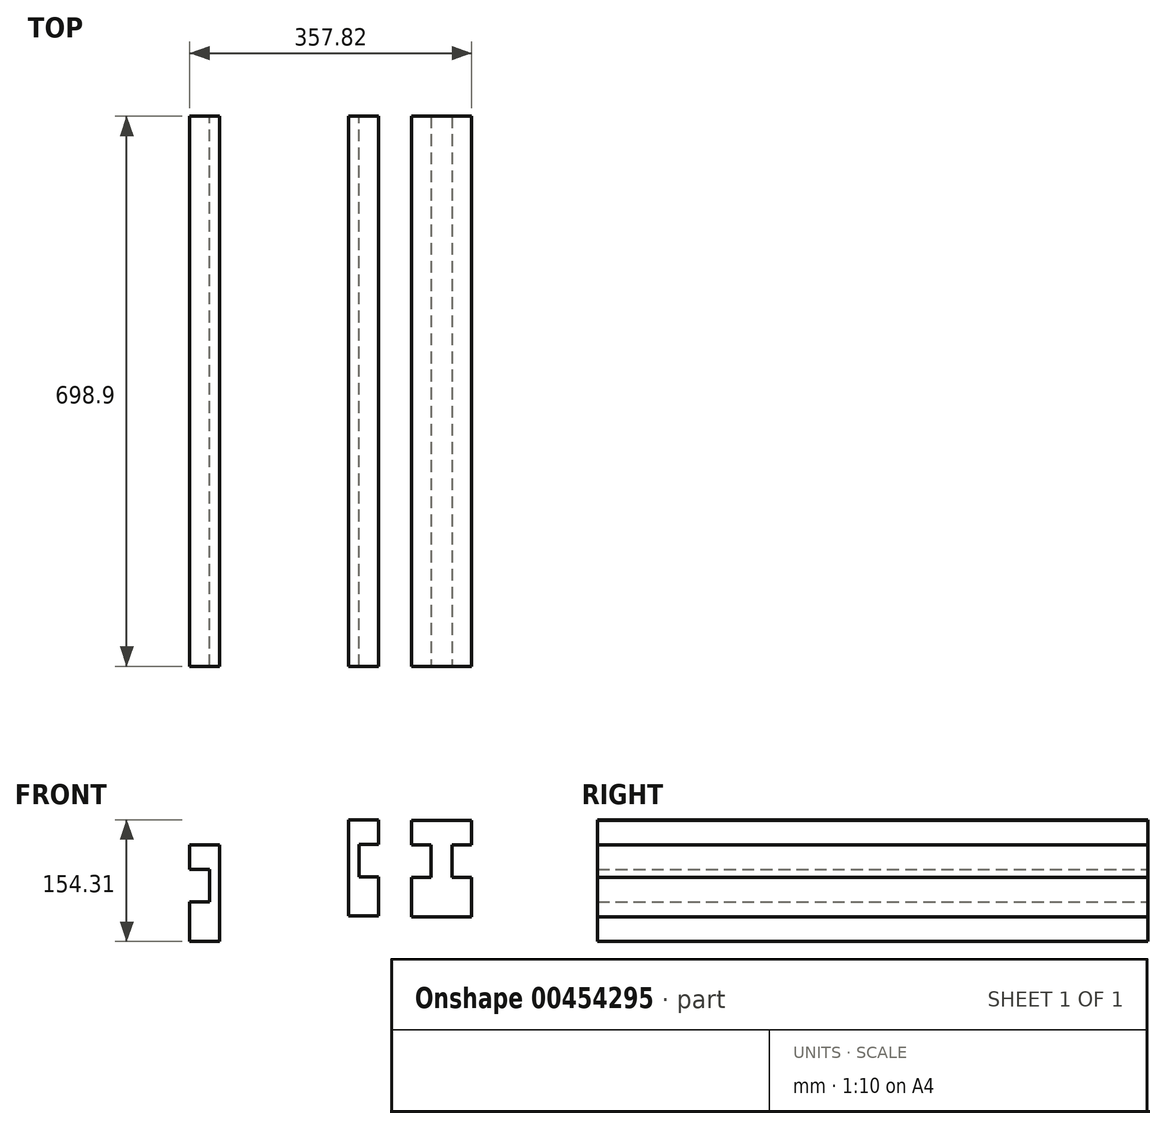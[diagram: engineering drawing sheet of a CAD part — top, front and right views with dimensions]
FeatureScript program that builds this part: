
annotation { "Feature Type Name" : "Feature", "Feature Type Description" : "" }
export const myFeature = defineFeature(function(context is Context, id is Id, definition is map)
    precondition{}
    {
        {
            var Q0;
            Q0=qCreatedBy(makeId("Front.planeOp"),FACE);
            var sketch = newSketch(context, id + "F0", { "sketchPlane" : qUnion([Q0])});
            skLineSegment(sketch, "E0.bottom", {"start": v(13.05, -61.15) * mm, "end": v(-13.05, -61.15) * mm});
            skLineSegment(sketch, "E0.top", {"start": v(13.05, 61.15) * mm, "end": v(-13.05, 61.15) * mm});
            skLineSegment(sketch, "E0.left", {"start": v(13.05, -61.15) * mm, "end": v(13.05, 61.15) * mm});
            skLineSegment(sketch, "E0.right", {"start": v(-13.05, -61.15) * mm, "end": v(-13.05, 61.15) * mm});
            skPoint(sketch, "E0.middle", {"position": v(0, 0) * mm});
            skSolve(sketch);
        }
        {
            var Q0;
            Q0=makeQuery(id+"F0.imprint","IMPRINT",FACE,{"disambiguationData":[TD([[makeQuery(id+"F0.imprint","IMPRINT",EDGE,{"derivedFrom":sQuery(id+"F0.wireOp",EDGE,"E0.bottom")}),-1.0]])]});
            extrude(context, id + "F1", {"entities" : qUnion([Q0]), "depth" : 698.9 * mm});
        }
        {
            var Q0;
            Q0=makeQuery(id+"F1.opExtrude","CAP_FACE",FACE,{"disambiguationData":[OSD([sQuery(id+"F0.wireOp",EDGE,"E0.bottom"),sQuery(id+"F0.wireOp",EDGE,"E0.top"),sQuery(id+"F0.wireOp",EDGE,"E0.left"),sQuery(id+"F0.wireOp",EDGE,"E0.right")])],"isStart":false});
            var sketch = newSketch(context, id + "F2", { "sketchPlane" : qUnion([Q0])});
            skLineSegment(sketch, "E1.bottom", {"start": v(-13.05, 61.15) * mm, "end": v(-38.05, 61.15) * mm});
            skLineSegment(sketch, "E2", {"start": v(0, 61.15) * mm, "end": v(0, -61.15) * mm, "construction": true});
            skPoint(sketch, "E3", {"position": v(-13.05, -11.15) * mm});
            skPoint(sketch, "E4", {"position": v(-13.05, 30.05) * mm});
            skLineSegment(sketch, "E5", {"start": v(-13.05, -61.15) * mm, "end": v(-38.05, -61.15) * mm});
            skLineSegment(sketch, "E6", {"start": v(-38.05, -61.15) * mm, "end": v(-38.05, -11.14) * mm});
            skLineSegment(sketch, "E7", {"start": v(-38.05, -11.14) * mm, "end": v(-13.05, -11.15) * mm});
            skLineSegment(sketch, "E8", {"start": v(-13.05, 30.05) * mm, "end": v(-38.05, 30.05) * mm});
            skLineSegment(sketch, "E9", {"start": v(-38.05, 30.05) * mm, "end": v(-38.05, 61.15) * mm});
            skLineSegment(sketch, "E10", {"start": v(-13.05, 61.15) * mm, "end": v(-13.05, 30.05) * mm});
            skLineSegment(sketch, "E11.MirrorCS", {"start": v(13.05, 61.15) * mm, "end": v(38.05, 61.15) * mm});
            skLineSegment(sketch, "E12.MirrorCS", {"start": v(38.05, 30.05) * mm, "end": v(38.05, 61.15) * mm});
            skLineSegment(sketch, "E13.MirrorCS", {"start": v(13.05, 30.05) * mm, "end": v(38.05, 30.05) * mm});
            skLineSegment(sketch, "E14.MirrorCS", {"start": v(13.05, 61.15) * mm, "end": v(13.05, 30.05) * mm});
            skLineSegment(sketch, "E15.MirrorCS", {"start": v(38.05, -11.14) * mm, "end": v(13.05, -11.15) * mm});
            skLineSegment(sketch, "E16.MirrorCS", {"start": v(38.05, -61.15) * mm, "end": v(38.05, -11.14) * mm});
            skLineSegment(sketch, "E17.MirrorCS", {"start": v(13.05, -61.15) * mm, "end": v(38.05, -61.15) * mm});
            skLineSegment(sketch, "E18", {"start": v(-13.05, -11.15) * mm, "end": v(-13.05, -61.15) * mm});
            skLineSegment(sketch, "E19", {"start": v(13.05, -11.15) * mm, "end": v(13.05, -61.15) * mm});
            skSolve(sketch);
        }
        {
            var Q0;
            Q0 = qSketchRegion(id + "F2", true);
            extrude(context, id + "F3", {"entities" : qUnion([Q0]), "operationType" : NewBodyOperationType.ADD, "oppositeDirection" : true, "depth" : 698.9 * mm});
        }
        {
            var Q0;
            Q0=qCreatedBy(makeId("Front.planeOp"),FACE);
            var sketch = newSketch(context, id + "F4", { "sketchPlane" : qUnion([Q0])});
            skLineSegment(sketch, "E20", {"start": v(-117.99, 62) * mm, "end": v(-117.99, -60.3) * mm, "construction": true});
            skLineSegment(sketch, "E21.MirrorCS", {"start": v(-79.94, 30.9) * mm, "end": v(-79.94, 62) * mm});
            skLineSegment(sketch, "E22.MirrorCS", {"start": v(-104.94, 30.9) * mm, "end": v(-79.94, 30.9) * mm});
            skLineSegment(sketch, "E23.MirrorCS", {"start": v(-79.94, -10.3) * mm, "end": v(-104.94, -10.3) * mm});
            skLineSegment(sketch, "E24.MirrorCS", {"start": v(-79.94, -60.3) * mm, "end": v(-79.94, -10.3) * mm});
            skLineSegment(sketch, "E25", {"start": v(-79.94, 62) * mm, "end": v(-117.99, 62) * mm});
            skLineSegment(sketch, "E26", {"start": v(-79.94, -60.3) * mm, "end": v(-117.99, -60.3) * mm});
            skLineSegment(sketch, "E27", {"start": v(-104.94, 30.9) * mm, "end": v(-104.94, -10.3) * mm});
            skLineSegment(sketch, "E28", {"start": v(-117.99, 62) * mm, "end": v(-117.99, -60.3) * mm});
            skSolve(sketch);
        }
        {
            var Q0;
            Q0 = qSketchRegion(id + "F4", true);
            extrude(context, id + "F5", {"entities" : qUnion([Q0]), "depth" : 698.9 * mm});
        }
        {
            var Q0;
            Q0=qCreatedBy(makeId("Front.planeOp"),FACE);
            var sketch = newSketch(context, id + "F6", { "sketchPlane" : qUnion([Q0])});
            skLineSegment(sketch, "E29", {"start": v(-281.72, 29.98) * mm, "end": v(-281.72, -92.32) * mm});
            skLineSegment(sketch, "E30.MirrorCS", {"start": v(-319.77, 29.98) * mm, "end": v(-281.72, 29.98) * mm});
            skLineSegment(sketch, "E31.MirrorCS", {"start": v(-319.77, -1.12) * mm, "end": v(-319.77, 29.98) * mm});
            skLineSegment(sketch, "E32.MirrorCS", {"start": v(-294.77, -1.12) * mm, "end": v(-319.77, -1.12) * mm});
            skLineSegment(sketch, "E33.MirrorCS", {"start": v(-294.77, -1.12) * mm, "end": v(-294.77, -42.32) * mm});
            skLineSegment(sketch, "E34.MirrorCS", {"start": v(-319.77, -42.3) * mm, "end": v(-294.77, -42.32) * mm});
            skLineSegment(sketch, "E35.MirrorCS", {"start": v(-319.77, -92.32) * mm, "end": v(-319.77, -42.3) * mm});
            skLineSegment(sketch, "E36.MirrorCS", {"start": v(-319.77, -92.32) * mm, "end": v(-281.72, -92.32) * mm});
            skSolve(sketch);
        }
        {
            var Q0;
            Q0 = qSketchRegion(id + "F6", true);
            extrude(context, id + "F7", {"entities" : qUnion([Q0]), "depth" : 698.9 * mm});
        }
    });
